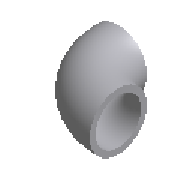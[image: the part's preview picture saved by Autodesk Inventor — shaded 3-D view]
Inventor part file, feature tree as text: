
AUTODESK INVENTOR PART (.ipt)
format: ipt  version: 2023.2 (Build 272271030, 271C)  size: 190,976 bytes
history: native  units: mm (DEFAULTED — no unit token found)
features: other x4, sketch x2, sweep x1
ambient origin geometry x8: Origin, YZ Plane, XZ Plane, XY Plane, X Axis, Y Axis, Z Axis, Center Point
bodies: Solid1 (feature_tree)
feature tree (7):
  sweep  "Sweep1"
  other  "Work Point1"
  other  "Work Axis1"
  other  "Work Point2"
  other  "Work Axis2"
  sketch  "Sketch1"  dims[d0=441.4mm d1=457.2mm]
  sketch  "Sketch2"  dims[d2=457.2mm d3=90.0deg d4=457.2mm d5=0.0mm d6=0.0mm]
